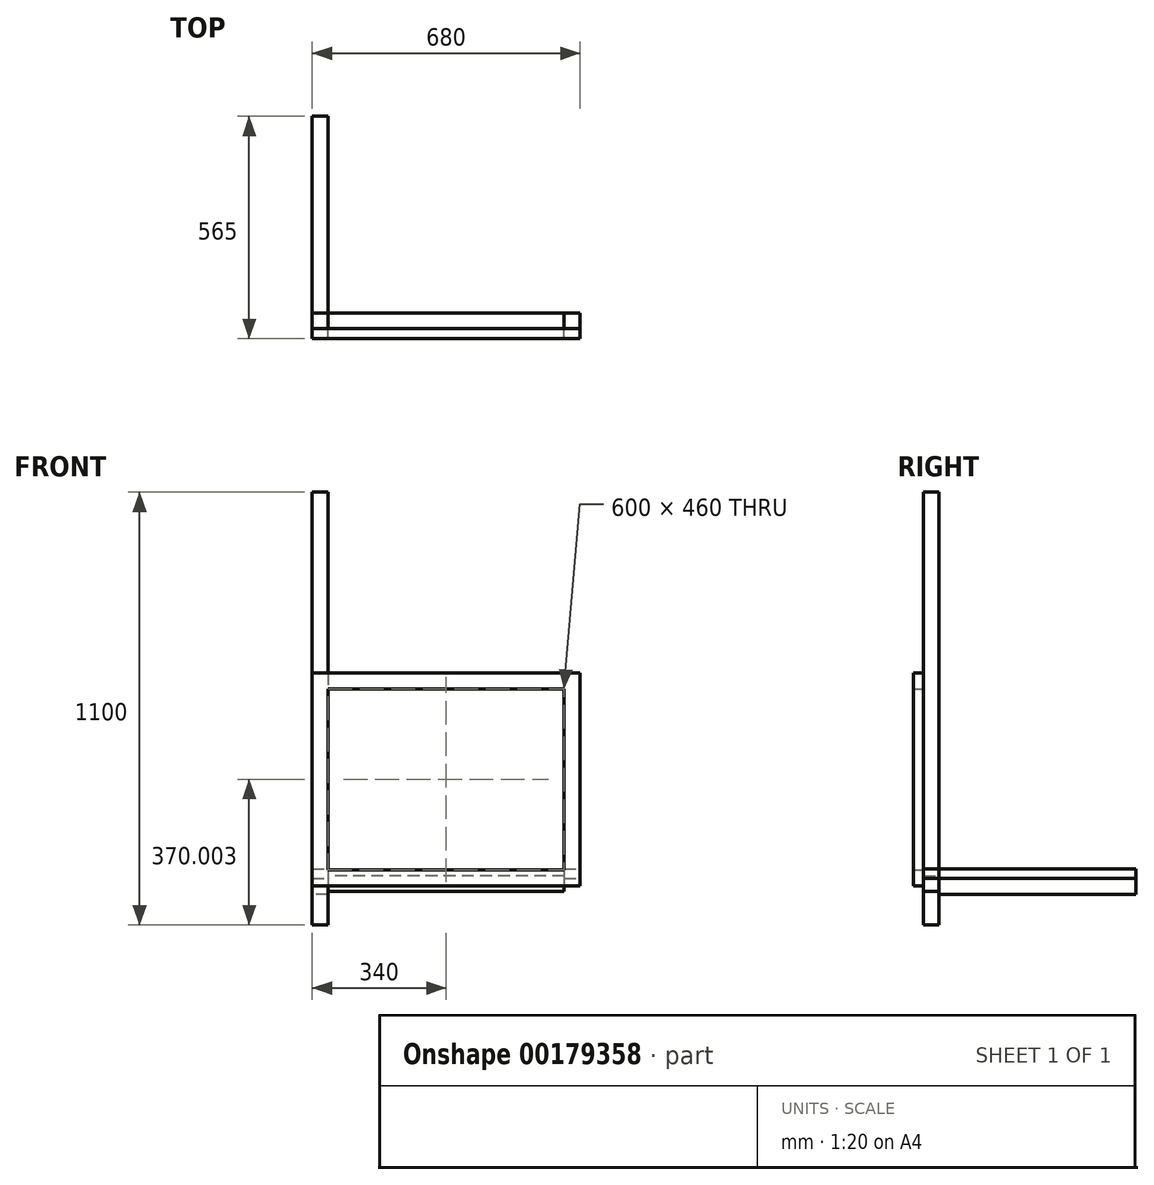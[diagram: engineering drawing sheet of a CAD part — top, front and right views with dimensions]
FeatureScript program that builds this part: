
annotation { "Feature Type Name" : "Feature", "Feature Type Description" : "" }
export const myFeature = defineFeature(function(context is Context, id is Id, definition is map)
    precondition{}
    {
        {
            var Q0;
            Q0=qCreatedBy(makeId("Top.planeOp"),FACE);
            var sketch = newSketch(context, id + "F0", { "sketchPlane" : qUnion([Q0])});
            skLineSegment(sketch, "E0.bottom", {"start": v(-20, 20) * mm, "end": v(20, 20) * mm});
            skLineSegment(sketch, "E0.top", {"start": v(-20, -20) * mm, "end": v(20, -20) * mm});
            skLineSegment(sketch, "E0.left", {"start": v(-20, 20) * mm, "end": v(-20, -20) * mm});
            skLineSegment(sketch, "E0.right", {"start": v(20, 20) * mm, "end": v(20, -20) * mm});
            skSolve(sketch);
        }
        {
            var Q0;
            Q0=makeQuery(id+"F0.imprint","IMPRINT",FACE,{"disambiguationData":[TD([[makeQuery(id+"F0.imprint","IMPRINT",EDGE,{"derivedFrom":sQuery(id+"F0.wireOp",EDGE,"E0.bottom")}),-1.0]])]});
            extrude(context, id + "F1", {"entities" : qUnion([Q0]), "depth" : 1100 * mm});
        }
        {
            var Q0;
            Q0=makeQuery(id+"F1.opExtrude","SWEPT_FACE",FACE,{"disambiguationData":[OSD([sQuery(id+"F0.wireOp",EDGE,"E0.right")])]});
            var sketch = newSketch(context, id + "F2", { "sketchPlane" : qUnion([Q0])});
            skLineSegment(sketch, "E1.bottom", {"start": v(-20, 125.37) * mm, "end": v(20, 125.37) * mm});
            skLineSegment(sketch, "E1.top", {"start": v(-20, 85.37) * mm, "end": v(20, 85.37) * mm});
            skLineSegment(sketch, "E1.left", {"start": v(-20, 125.37) * mm, "end": v(-20, 85.37) * mm});
            skLineSegment(sketch, "E1.right", {"start": v(20, 125.37) * mm, "end": v(20, 85.37) * mm});
            skSolve(sketch);
        }
        {
            var Q0;
            Q0=makeQuery(id+"F2.imprint","IMPRINT",FACE,{"disambiguationData":[TD([[makeQuery(id+"F2.imprint","IMPRINT",EDGE,{"derivedFrom":sQuery(id+"F2.wireOp",EDGE,"E1.bottom")}),-1.0]])]});
            extrude(context, id + "F3", {"entities" : qUnion([Q0]), "depth" : 600 * mm});
        }
        {
            var Q0;
            Q0=makeQuery(id+"F1.opExtrude","SWEPT_FACE",FACE,{"disambiguationData":[OSD([sQuery(id+"F0.wireOp",EDGE,"E0.bottom")])]});
            var sketch = newSketch(context, id + "F4", { "sketchPlane" : qUnion([Q0])});
            skLineSegment(sketch, "E2.bottom", {"start": v(-20, 118) * mm, "end": v(20, 118) * mm});
            skLineSegment(sketch, "E2.top", {"start": v(-20, 78) * mm, "end": v(20, 78) * mm});
            skLineSegment(sketch, "E2.left", {"start": v(-20, 118) * mm, "end": v(-20, 78) * mm});
            skLineSegment(sketch, "E2.right", {"start": v(20, 118) * mm, "end": v(20, 78) * mm});
            skSolve(sketch);
        }
        {
            var Q0;
            Q0=makeQuery(id+"F4.imprint","IMPRINT",FACE,{"disambiguationData":[TD([[makeQuery(id+"F4.imprint","IMPRINT",EDGE,{"derivedFrom":sQuery(id+"F4.wireOp",EDGE,"E2.bottom")}),-1.0]])]});
            extrude(context, id + "F5", {"entities" : qUnion([Q0]), "depth" : 500 * mm});
        }
        {
            var Q0;
            Q0=makeQuery(id+"F5.opExtrude","SWEPT_FACE",FACE,{"disambiguationData":[OSD([sQuery(id+"F4.wireOp",EDGE,"E2.bottom")])]});
            var sketch = newSketch(context, id + "F6", { "sketchPlane" : qUnion([Q0])});
            skLineSegment(sketch, "E3.bottom", {"start": v(-20, -20) * mm, "end": v(660, -20) * mm});
            skLineSegment(sketch, "E3.top", {"start": v(-20, 560) * mm, "end": v(660, 560) * mm});
            skLineSegment(sketch, "E3.left", {"start": v(-20, -20) * mm, "end": v(-20, 560) * mm});
            skLineSegment(sketch, "E3.right", {"start": v(660, -20) * mm, "end": v(660, 560) * mm});
            skLineSegment(sketch, "E4.bottom", {"start": v(-20, -20) * mm, "end": v(20, -20) * mm});
            skLineSegment(sketch, "E4.top", {"start": v(-20, 20) * mm, "end": v(20, 20) * mm});
            skLineSegment(sketch, "E4.left", {"start": v(-20, -20) * mm, "end": v(-20, 20) * mm});
            skLineSegment(sketch, "E4.right", {"start": v(20, -20) * mm, "end": v(20, 20) * mm});
            skLineSegment(sketch, "E5.bottom", {"start": v(-20, 560) * mm, "end": v(20, 560) * mm});
            skLineSegment(sketch, "E5.top", {"start": v(-20, 520) * mm, "end": v(20, 520) * mm});
            skLineSegment(sketch, "E5.left", {"start": v(-20, 560) * mm, "end": v(-20, 520) * mm});
            skLineSegment(sketch, "E5.right", {"start": v(20, 560) * mm, "end": v(20, 520) * mm});
            skLineSegment(sketch, "E6.bottom", {"start": v(660, 560) * mm, "end": v(620, 560) * mm});
            skLineSegment(sketch, "E6.top", {"start": v(660, 520) * mm, "end": v(620, 520) * mm});
            skLineSegment(sketch, "E6.left", {"start": v(660, 560) * mm, "end": v(660, 520) * mm});
            skLineSegment(sketch, "E6.right", {"start": v(620, 560) * mm, "end": v(620, 520) * mm});
            skLineSegment(sketch, "E7.bottom", {"start": v(660, -20) * mm, "end": v(620, -20) * mm});
            skLineSegment(sketch, "E7.top", {"start": v(660, 20) * mm, "end": v(620, 20) * mm});
            skLineSegment(sketch, "E7.left", {"start": v(660, -20) * mm, "end": v(660, 20) * mm});
            skLineSegment(sketch, "E7.right", {"start": v(620, -20) * mm, "end": v(620, 20) * mm});
            skSolve(sketch);
        }
        {
            var Q0;
            Q0=makeQuery(id+"F6.imprint","IMPRINT",FACE,{"disambiguationData":[TD([[makeQuery(id+"F6.imprint","IMPRINT",EDGE,{"derivedFrom":sQuery(id+"F6.wireOp",EDGE,"E3.left")}),1.0]])]});
            var Q1;
            Q1=makeQuery(id+"F6.imprint","IMPRINT",FACE,{"disambiguationData":[TD([[makeQuery(id+"F6.imprint","IMPRINT",EDGE,{"derivedFrom":sQuery(id+"F6.wireOp",EDGE,"E3.bottom")}),1.0]])]});
            extrude(context, id + "F7", {"entities" : qUnion([Q0, Q1]), "depth" : 25 * mm});
        }
        {
            var Q0;
            Q0=makeQuery(id+"F1.opExtrude","SWEPT_FACE",FACE,{"disambiguationData":[OSD([sQuery(id+"F0.wireOp",EDGE,"E0.top")])]});
            var sketch = newSketch(context, id + "F8", { "sketchPlane" : qUnion([Q0])});
            skLineSegment(sketch, "E8.bottom", {"start": v(-20, 100) * mm, "end": v(660, 100) * mm});
            skLineSegment(sketch, "E8.top", {"start": v(-20, 640) * mm, "end": v(660, 640) * mm});
            skLineSegment(sketch, "E8.left", {"start": v(-20, 100) * mm, "end": v(-20, 640) * mm});
            skLineSegment(sketch, "E8.right", {"start": v(660, 100) * mm, "end": v(660, 640) * mm});
            skLineSegment(sketch, "E9.0", {"start": v(20, 600) * mm, "end": v(620, 600) * mm});
            skLineSegment(sketch, "E9.1", {"start": v(20, 140) * mm, "end": v(20, 600) * mm});
            skLineSegment(sketch, "E9.2", {"start": v(20, 140) * mm, "end": v(620, 140) * mm});
            skLineSegment(sketch, "E9.3", {"start": v(620, 140) * mm, "end": v(620, 600) * mm});
            skSolve(sketch);
        }
        {
            var Q0;
            Q0 = qSketchRegion(id + "F8", true);
            extrude(context, id + "F9", {"entities" : qUnion([Q0]), "depth" : 25 * mm});
        }
    });
